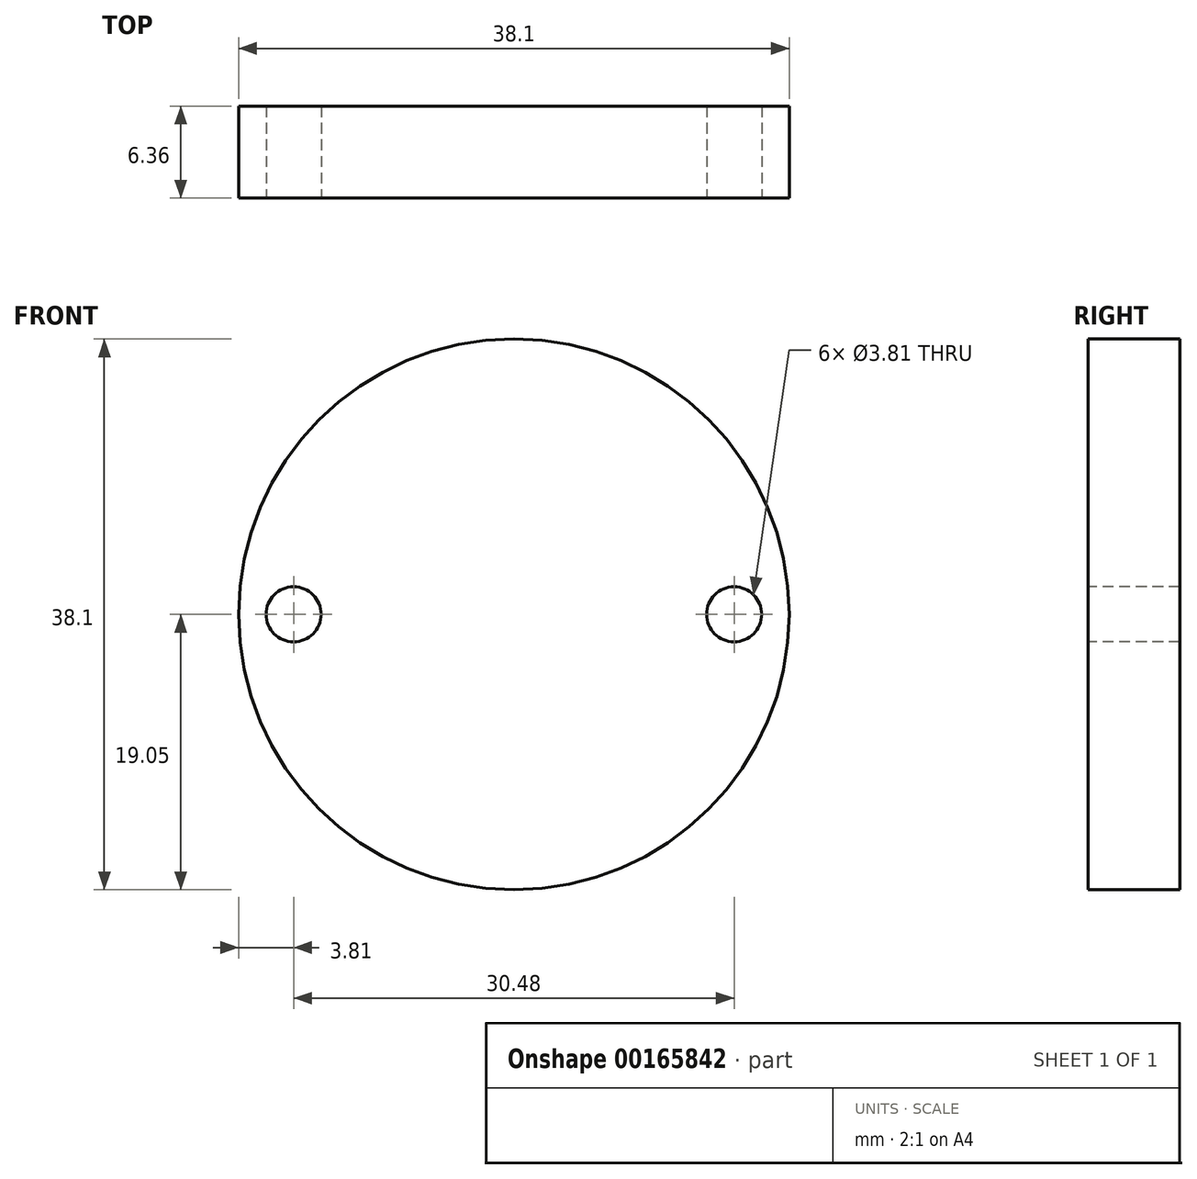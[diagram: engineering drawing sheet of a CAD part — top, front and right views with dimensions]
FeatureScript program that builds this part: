
annotation { "Feature Type Name" : "Feature", "Feature Type Description" : "" }
export const myFeature = defineFeature(function(context is Context, id is Id, definition is map)
    precondition{}
    {
        {
            var Q0;
            Q0=qCreatedBy(makeId("Front.planeOp"),FACE);
            var sketch = newSketch(context, id + "F0", { "sketchPlane" : qUnion([Q0])});
            skCircle(sketch, "E0", {"center": v(0, 0) * mm, "radius": 19.05 * mm});
            skPoint(sketch, "E1", {"position": v(-15.24, 0) * mm});
            skPoint(sketch, "E2", {"position": v(15.24, 0) * mm});
            skSolve(sketch);
        }
        {
            var Q0;
            Q0 = qSketchRegion(id + "F0", true);
            extrude(context, id + "F1", {"entities" : qUnion([Q0]), "endBound" : BoundingType.SYMMETRIC, "depth" : 6.35 * mm});
        }
        {
            var Q0;
            Q0=sQuery(id+"F0.wireOp",VERTEX,"E2");
            var Q1;
            Q1=sQuery(id+"F0.wireOp",VERTEX,"E1");
            var Q2;
            Q2=makeQuery(id+"F1.opExtrude","SWEPT_BODY",BODY,{"disambiguationData":[OSD([sQuery(id+"F0.wireOp",EDGE,"E0")])]});
            hole(context, id + "F2", {"style" : HoleStyle.SIMPLE, "endStyle" : HoleEndStyle.THROUGH, "holeDiameter" : 3.8 * mm, "startFromSketch" : true, "locations" : qUnion([Q0, Q1]), "scope" : qUnion([Q2]), "isTappedThrough" : true});
        }
        {
            var Q0;
            Q0=sQuery(id+"F0.wireOp",VERTEX,"E1");
            var Q1;
            Q1=sQuery(id+"F0.wireOp",VERTEX,"E2");
            var Q2;
            Q2=makeQuery(id+"F1.opExtrude","SWEPT_BODY",BODY,{"disambiguationData":[OSD([sQuery(id+"F0.wireOp",EDGE,"E0")])]});
            hole(context, id + "F3", {"style" : HoleStyle.SIMPLE, "endStyle" : HoleEndStyle.THROUGH, "oppositeDirection" : true, "holeDiameter" : 3.8 * mm, "startFromSketch" : true, "locations" : qUnion([Q0, Q1]), "scope" : qUnion([Q2]), "isTappedThrough" : true});
        }
    });
